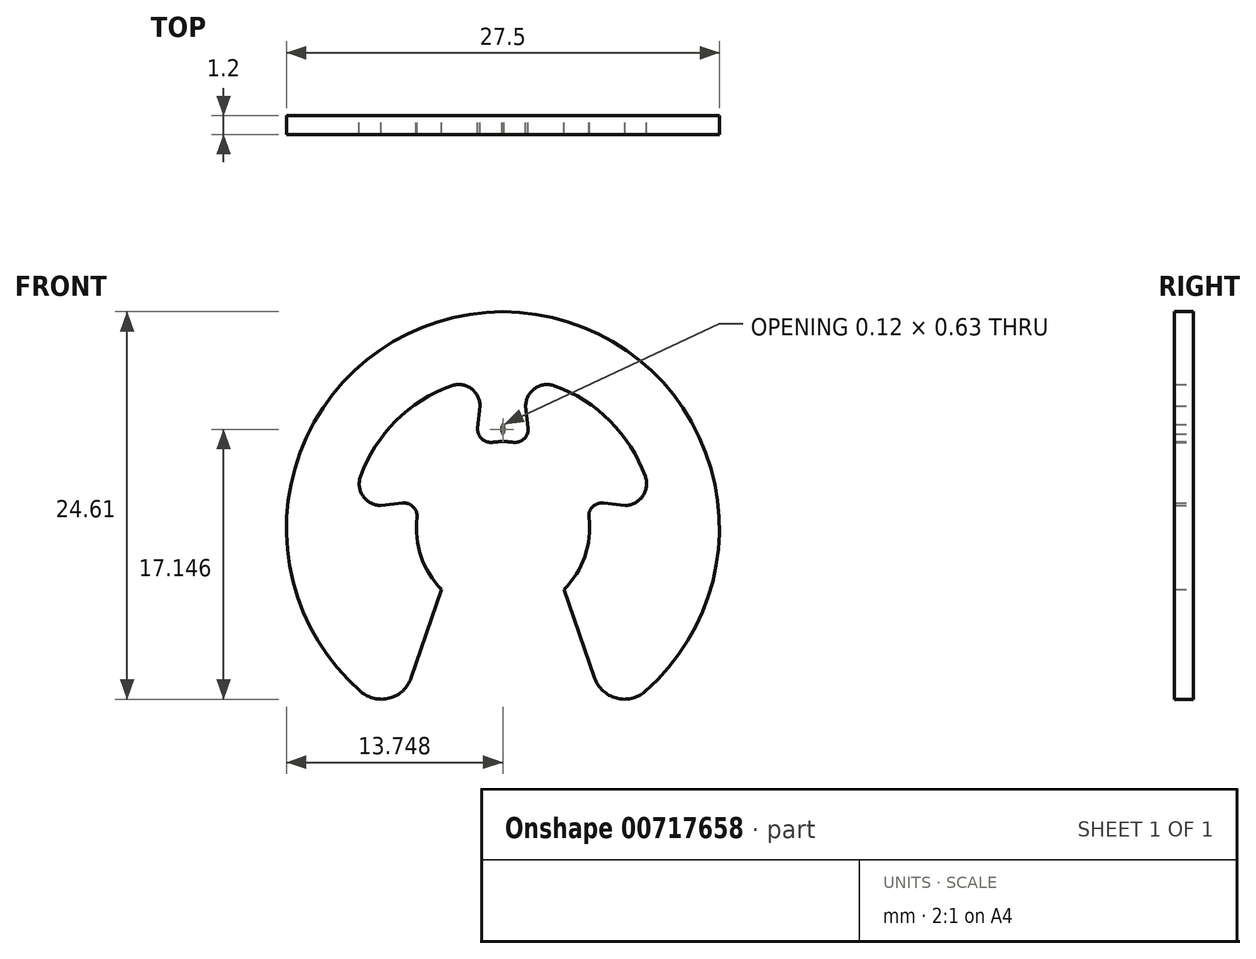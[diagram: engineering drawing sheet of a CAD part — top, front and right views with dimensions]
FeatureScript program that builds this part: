
annotation { "Feature Type Name" : "Feature", "Feature Type Description" : "" }
export const myFeature = defineFeature(function(context is Context, id is Id, definition is map)
    precondition{}
    {
        {
            var Q0;
            Q0=qCreatedBy(makeId("Front.planeOp"),FACE);
            var sketch = newSketch(context, id + "F0", { "sketchPlane" : qUnion([Q0])});
            skLineSegment(sketch, "E0", {"start": v(-62.9, 34.75) * mm, "end": v(-62.9, -35.9) * mm, "construction": true});
            skLineSegment(sketch, "E1", {"start": v(-34.1, 0) * mm, "end": v(-106.3, 0) * mm, "construction": true});
            skArc(sketch, "E2", {"start": v(-56.2, -12.01) * mm, "mid": v(-62.9, 13.75) * mm, "end": v(-69.58, -12.01) * mm});
            skArc(sketch, "E3", {"start": v(-66.18, 9.04) * mm, "mid": v(-69.7, 6.8) * mm, "end": v(-71.94, 3.3) * mm});
            skArc(sketch, "E4", {"start": v(-68.35, 0.67) * mm, "mid": v(-68.1, -1.8) * mm, "end": v(-66.78, -3.89) * mm});
            skArc(sketch, "E5", {"start": v(-62.9, 6.6) * mm, "mid": v(-62.95, 6.29) * mm, "end": v(-62.9, 5.97) * mm});
            skArc(sketch, "E6.MirrorC", {"start": v(-62.9, 6.6) * mm, "mid": v(-62.83, 6.29) * mm, "end": v(-62.9, 5.97) * mm});
            skLineSegment(sketch, "E7", {"start": v(-62.12, 6.29) * mm, "end": v(-62.9, 0) * mm, "construction": true});
            skArc(sketch, "E8", {"start": v(-59.6, 9.04) * mm, "mid": v(-60.86, 8.88) * mm, "end": v(-61.45, 7.75) * mm});
            skLineSegment(sketch, "E9", {"start": v(-62.9, 0) * mm, "end": v(-60.07, 7.75) * mm, "construction": true});
            skArc(sketch, "E10.MirrorC", {"start": v(-66.18, 9.04) * mm, "mid": v(-64.92, 8.88) * mm, "end": v(-64.34, 7.75) * mm});
            skLineSegment(sketch, "E11", {"start": v(-61.45, 7.75) * mm, "end": v(-61.3, 6.38) * mm});
            skLineSegment(sketch, "E12.MirrorCS", {"start": v(-64.34, 7.75) * mm, "end": v(-64.5, 6.38) * mm});
            skArc(sketch, "E13.trimOffspring", {"start": v(-62.22, 5.46) * mm, "mid": v(-61.53, 5.7) * mm, "end": v(-61.3, 6.38) * mm});
            skArc(sketch, "E14.trimOffspring", {"start": v(-63.56, 5.46) * mm, "mid": v(-64.25, 5.7) * mm, "end": v(-64.5, 6.38) * mm});
            skLineSegment(sketch, "E15", {"start": v(-90.57, 27.68) * mm, "end": v(-38.24, -24.65) * mm, "construction": true});
            skArc(sketch, "E16.MirrorCS", {"start": v(-71.94, 3.3) * mm, "mid": v(-71.77, 2.03) * mm, "end": v(-70.64, 1.45) * mm});
            skLineSegment(sketch, "E17.MirrorCS", {"start": v(-70.64, 1.45) * mm, "end": v(-69.27, 1.6) * mm});
            skArc(sketch, "E18.MirrorCS", {"start": v(-68.35, 0.67) * mm, "mid": v(-68.59, 1.36) * mm, "end": v(-69.27, 1.6) * mm});
            skArc(sketch, "E19.MirrorCS", {"start": v(-53.85, 3.3) * mm, "mid": v(-54.01, 2.03) * mm, "end": v(-55.14, 1.45) * mm});
            skLineSegment(sketch, "E20.MirrorCS", {"start": v(-55.14, 1.45) * mm, "end": v(-56.51, 1.6) * mm});
            skArc(sketch, "E21.MirrorCS", {"start": v(-57.43, 0.67) * mm, "mid": v(-57.2, 1.36) * mm, "end": v(-56.51, 1.6) * mm});
            skArc(sketch, "E22.trimOffspring", {"start": v(-56.09, -6.8) * mm, "mid": v(-54, -3.68) * mm, "end": v(-53.27, 0) * mm});
            skArc(sketch, "E23.trimOffspring", {"start": v(-53.85, 3.3) * mm, "mid": v(-56.09, 6.8) * mm, "end": v(-59.6, 9.04) * mm});
            skArc(sketch, "E24.trimOffspring", {"start": v(-62.22, 5.46) * mm, "mid": v(-62.9, 5.5) * mm, "end": v(-63.56, 5.46) * mm});
            skLineSegment(sketch, "E25", {"start": v(-59, -3.89) * mm, "end": v(-56.2, -12.01) * mm});
            skLineSegment(sketch, "E26.MirrorCS", {"start": v(-66.78, -3.89) * mm, "end": v(-69.58, -12.01) * mm});
            skArc(sketch, "E27.trimOffspring", {"start": v(-59, -3.89) * mm, "mid": v(-57.7, -1.8) * mm, "end": v(-57.43, 0.67) * mm});
            skSolve(sketch);
        }
        {
            var Q0;
            Q0=makeQuery(id+"F0.imprint","IMPRINT",FACE,{"disambiguationData":[TD([[makeQuery(id+"F0.imprint","IMPRINT",EDGE,{"derivedFrom":sQuery(id+"F0.wireOp",EDGE,"E2")}),1.0]])]});
            extrude(context, id + "F1", {"entities" : qUnion([Q0]), "depth" : 1.2 * mm, "offsetDistance" : 25 * mm});
        }
        {
            var Q0;
            Q0=makeQuery(id+"F1.opExtrude","SWEPT_EDGE",EDGE,{"disambiguationData":[OSD([sQuery(id+"F0.wireOp",EDGE,"E2"),sQuery(id+"F0.wireOp",EDGE,"E26.MirrorCS")])]});
            var Q1;
            Q1=makeQuery(id+"F1.opExtrude","SWEPT_EDGE",EDGE,{"disambiguationData":[OSD([sQuery(id+"F0.wireOp",EDGE,"E2"),sQuery(id+"F0.wireOp",EDGE,"E25")])]});
            fillet(context, id + "F2", {"entities" : qUnion([Q0, Q1]), "radius" : 2 * mm, "tangentPropagation" : true, "allowEdgeOverflow" : false});
        }
    });
